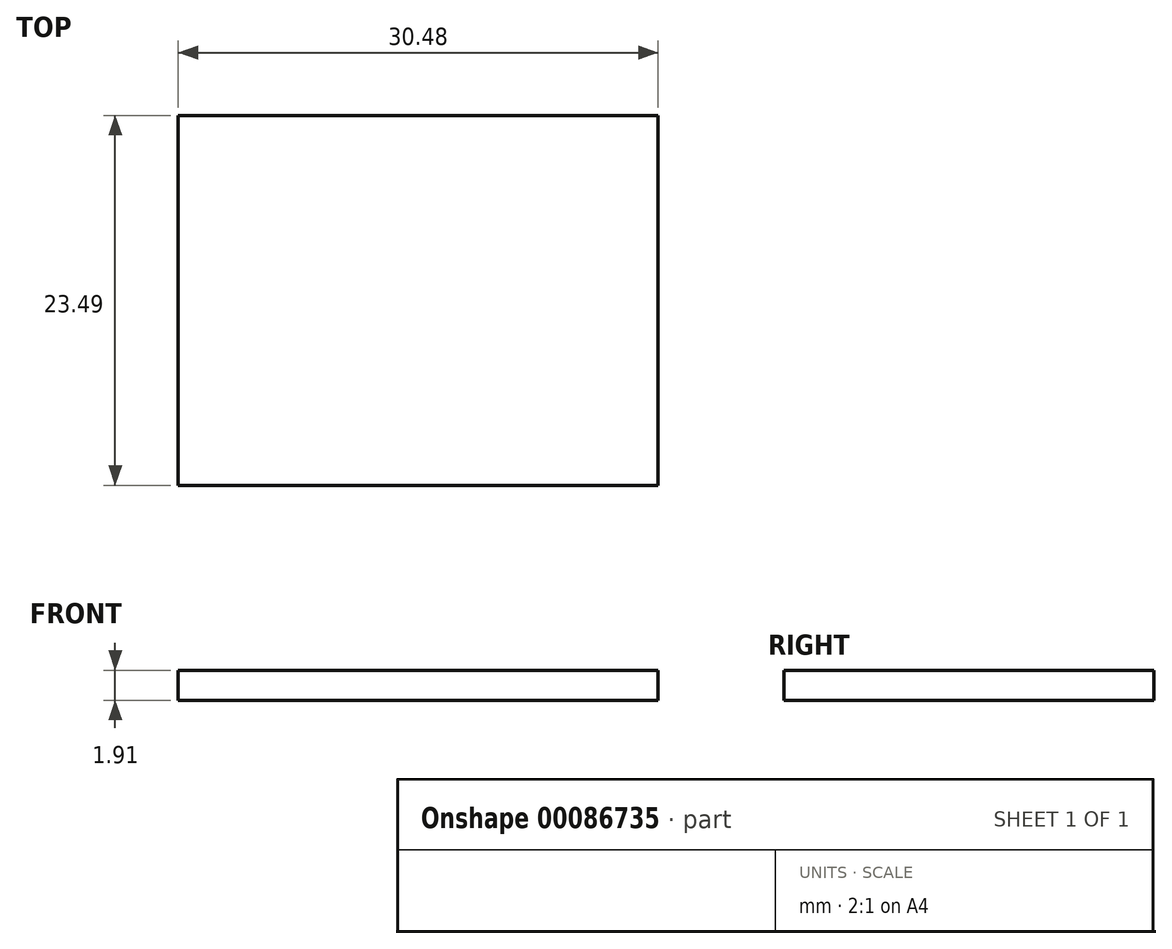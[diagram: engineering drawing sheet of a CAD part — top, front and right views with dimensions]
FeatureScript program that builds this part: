
annotation { "Feature Type Name" : "Feature", "Feature Type Description" : "" }
export const myFeature = defineFeature(function(context is Context, id is Id, definition is map)
    precondition{}
    {
        {
            var Q0;
            Q0=qCreatedBy(makeId("Top.planeOp"),FACE);
            var sketch = newSketch(context, id + "F0", { "sketchPlane" : qUnion([Q0])});
            skLineSegment(sketch, "E0.bottom", {"start": v(0, 0) * mm, "end": v(30.48, 0) * mm});
            skLineSegment(sketch, "E0.top", {"start": v(0, 23.5) * mm, "end": v(30.48, 23.5) * mm});
            skLineSegment(sketch, "E0.left", {"start": v(0, 0) * mm, "end": v(0, 23.5) * mm});
            skLineSegment(sketch, "E0.right", {"start": v(30.48, 0) * mm, "end": v(30.48, 23.5) * mm});
            skSolve(sketch);
        }
        {
            var Q0;
            Q0=makeQuery(id+"F0.imprint","IMPRINT",FACE,{"disambiguationData":[TD([[makeQuery(id+"F0.imprint","IMPRINT",EDGE,{"derivedFrom":sQuery(id+"F0.wireOp",EDGE,"E0.bottom")}),1.0]])]});
            extrude(context, id + "F1", {"entities" : qUnion([Q0]), "depth" : 1.9 * mm});
        }
    });
